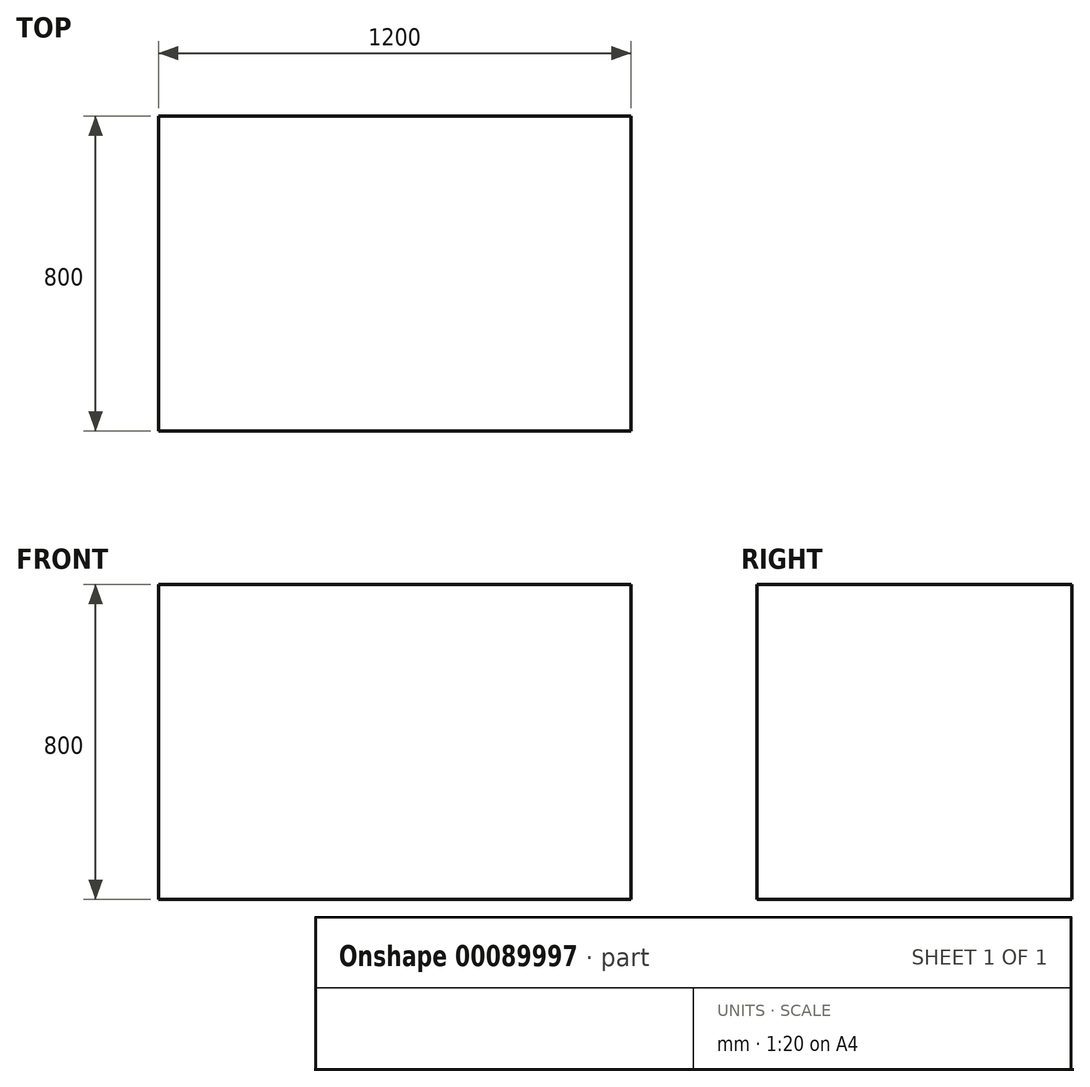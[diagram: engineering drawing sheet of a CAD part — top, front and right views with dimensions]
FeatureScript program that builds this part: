
annotation { "Feature Type Name" : "Feature", "Feature Type Description" : "" }
export const myFeature = defineFeature(function(context is Context, id is Id, definition is map)
    precondition{}
    {
        {
            var Q0;
            Q0=qCreatedBy(makeId("Top.planeOp"),FACE);
            var sketch = newSketch(context, id + "F0", { "sketchPlane" : qUnion([Q0])});
            skLineSegment(sketch, "E0.bottom", {"start": v(0, 0) * mm, "end": v(1200, 0) * mm});
            skLineSegment(sketch, "E0.top", {"start": v(0, 800) * mm, "end": v(1200, 800) * mm});
            skLineSegment(sketch, "E0.left", {"start": v(0, 0) * mm, "end": v(0, 800) * mm});
            skLineSegment(sketch, "E0.right", {"start": v(1200, 0) * mm, "end": v(1200, 800) * mm});
            skSolve(sketch);
        }
        {
            var Q0;
            Q0 = qSketchRegion(id + "F0", true);
            extrude(context, id + "F1", {"entities" : qUnion([Q0]), "depth" : 800 * mm});
        }
    });
